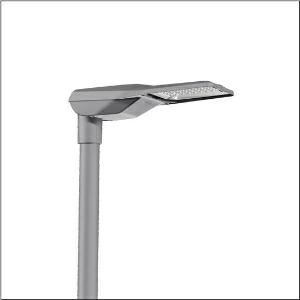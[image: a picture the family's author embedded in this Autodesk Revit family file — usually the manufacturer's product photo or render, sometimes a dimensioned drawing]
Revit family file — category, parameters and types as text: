
# Revit family: streetlight_sl_21_iq_mini___st1_0a_5xe2d41g08hb_63a2
name_source: partatom
category: Lighting Fixtures
units: mm (PartAtom-declared; Revit-internal decimal feet)

## family parameters
Cut with Voids When Loaded = No
Host = Face
Light Source = No
Part Type = Normal
Room Calculation Point = No
Round Connector Dimension = Use Diameter
Shared = No

## types (1)
- --- (1 x LED, 9860 lm, 70.9 W, 4000K)
    Apparent Load = 71 VA
    CIE Flux Codes = 37 72 97 100 100
    Color Rendering = 70
    Color Temperature = 4000K
    Default Elevation = 1800 mm
    Description = Streetlight SL 21 iQ mini, mast luminaire, primary light control with lens, of PMMA, primary optical cover: cover, of toughened safety glass, transparent, light distribution: ST1.0a, light emission: direct distribution, primary light characteristic: asymmetric, installation type: post-top, side-entry, LED, High Power LED, rated luminous flux: 9.860lm, luminous efficacy: 139lm/W, light colour: 740, colour temperature: 4000K, control: Street-Remote, Auto-Match, Temp-Guard, Lumen-Switch, Night-Set, Smart-Wire, Light-Fading, Desk-Remote (wireless, voltage-free reading and setting of iQ features in the workshop via application-optimized NFC function/RFID function), optimised constant luminous flux control (CLO 2.0), pre-setting: linear dimming characteristic, mains connection: 220..240V, AC, 50/60Hz, start of lifetime: 71W, end of service life: 75W, reduction: 31W, luminaire housing, of diecast aluminium, powder-coated, Siteco® metallic grey (DB 702S), corrosivity category C5 mid according to DIN EN ISO 12944, please order mast flange separately, inclination adjustable: 0°, 5°, 10°, 15°, sealing non-destructively replaceable, multi-level sealing system, length: 628mm, width: 235mm, height: 110mm, mast flange for spigot size: 42mm (side-entry): 5XC10008XM4, 60/48mm (side-entry/post-top): 5XC10108XM2, 76/60mm (side-entry/post-top): 5XC10108XM1, protection rating (complete): IP66, insulation class (complete): insulation class II (safety insulation), certification: CE, ENEC, ENEC+, VDE, impact resistance: IK09, permissible operating ambient temperature for outdoor applications: -40..+50°C, standard-compliant lighting for roads and squares, packaging unit: 1 piece

Light Distribution: ST1.0a
    Height = 110 mm
    Lamp = 1 x LED
    Lamp Light Flux = 9860 lm
    Lamp Power = 70.9 W
    Lamp count = 1
    Length = 625 mm
    Luminous efficacy = 139 lm/W
    Manufacturer = Siteco
    ModVariant = No
    Model = 5XE2D41G08HB
    Number of Poles = 1
    OnlyDefault = Yes
    Power Factor = 1
    Product Name = Streetlight SL 21 iQ mini | ST1.0a
    Product group = mast luminaire | pylon top
    ProductGroupID = 6100
    Protection Class = Protection class II
    Protection Degree = IP 66
    RLX_Detail_Level = 1
    RLX_Emergency_Light_Flux = 0 lm
    RLX_Emergency_Type = 0
    RLX_Emergency_Type_DB = No
    RlxData = <blob elided: 92189 chars, md5=906a738d>
    Socket = socket
    Standby Power = 0 W
    System Light Flux = 9860 lm
    System Power = 71 W
    Type Comments = factory setting: luminous flux: 100 % | dim-lin: 254 | 711 mA
    Type Image = l_1003519.jpg
    URL = http://relux.com
    VarID = @adj_128407
    Voltage = 0 V
    Weight = 0.00 kg
    Width = 234 mm

## geometry (parser evidence)
native form markers: Blend x4, Sweep x12
no freeform markers — native parametric forms only
